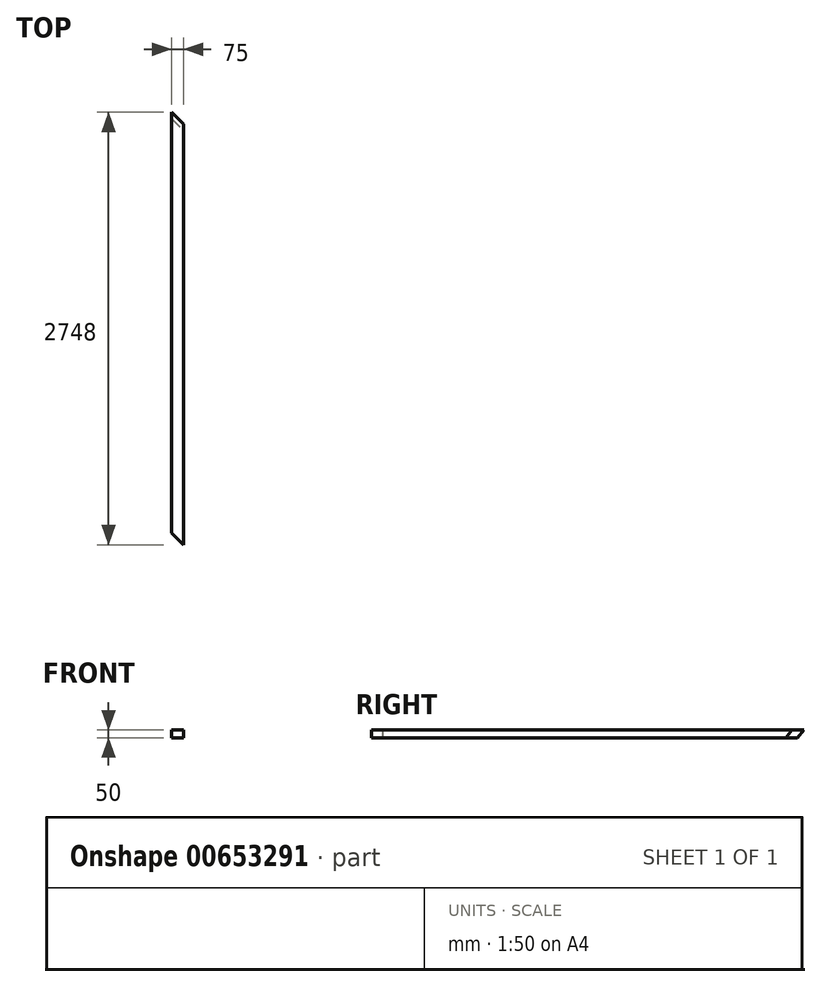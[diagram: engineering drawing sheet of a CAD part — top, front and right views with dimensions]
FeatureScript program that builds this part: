
annotation { "Feature Type Name" : "Feature", "Feature Type Description" : "" }
export const myFeature = defineFeature(function(context is Context, id is Id, definition is map)
    precondition{}
    {
        {
            var Q0;
            Q0=qCreatedBy(makeId("Front.planeOp"),FACE);
            var sketch = newSketch(context, id + "F0", { "sketchPlane" : qUnion([Q0])});
            skLineSegment(sketch, "E0.bottom", {"start": v(0, 0) * mm, "end": v(75, 0) * mm});
            skLineSegment(sketch, "E0.top", {"start": v(0, 50) * mm, "end": v(75, 50) * mm});
            skLineSegment(sketch, "E0.left", {"start": v(0, 0) * mm, "end": v(0, 50) * mm});
            skLineSegment(sketch, "E0.right", {"start": v(75, 0) * mm, "end": v(75, 50) * mm});
            skSolve(sketch);
        }
        {
            var Q0;
            Q0=makeQuery(id+"F0.imprint","IMPRINT",FACE,{"disambiguationData":[TD([[makeQuery(id+"F0.imprint","IMPRINT",EDGE,{"derivedFrom":sQuery(id+"F0.wireOp",EDGE,"E0.bottom")}),1.0]])]});
            extrude(context, id + "F1", {"entities" : qUnion([Q0]), "depth" : 2698 * mm + 50 * mm, "offsetDistance" : 25 * mm, "symmetric" : true});
        }
        {
            var Q0;
            Q0=makeQuery(id+"F1.opExtrude","SWEPT_FACE",FACE,{"disambiguationData":[OSD([sQuery(id+"F0.wireOp",EDGE,"E0.top")])]});
            var sketch = newSketch(context, id + "F2", { "sketchPlane" : qUnion([Q0])});
            skLineSegment(sketch, "E1", {"start": v(75, -1374) * mm, "end": v(0, -1299) * mm});
            skLineSegment(sketch, "E2.0", {"start": v(0, -1374) * mm, "end": v(75, -1374) * mm});
            skLineSegment(sketch, "E3.0", {"start": v(0, -1374) * mm, "end": v(0, 1374) * mm});
            skLineSegment(sketch, "E4", {"start": v(0, 1374) * mm, "end": v(75, 1299) * mm});
            skSolve(sketch);
        }
        {
            var Q0;
            {var subQ0=sQuery(id+"F2.wireOp",EDGE,"E4");Q0=makeQuery(id+"F2.imprint","IMPRINT",FACE,{"disambiguationData":[TD([[makeQuery(id+"F2.imprint","IMPRINT",EDGE,{"derivedFrom":subQ0}),1.0]])]});}
            var Q1;
            {var subQ0=sQuery(id+"F2.wireOp",EDGE,"E1");Q1=makeQuery(id+"F2.imprint","IMPRINT",FACE,{"disambiguationData":[TD([[makeQuery(id+"F2.imprint","IMPRINT",EDGE,{"derivedFrom":subQ0}),1.0]])]});}
            extrude(context, id + "F3", {"entities" : qUnion([Q0, Q1]), "operationType" : NewBodyOperationType.REMOVE, "endBound" : BoundingType.THROUGH_ALL, "oppositeDirection" : true, "depth" : 25 * mm, "offsetDistance" : 25 * mm});
        }
        {
            var Q0;
            Q0=makeQuery(id+"F1.opExtrude","SWEPT_FACE",FACE,{"disambiguationData":[OSD([sQuery(id+"F0.wireOp",EDGE,"E0.left")])]});
            var sketch = newSketch(context, id + "F4", { "sketchPlane" : qUnion([Q0])});
            skLineSegment(sketch, "E5", {"start": v(-1374, 50) * mm, "end": v(-1333.51, 0) * mm});
            skSolve(sketch);
        }
        {
            var Q0;
            {var subQ0=sQuery(id+"F4.wireOp",EDGE,"E5");Q0=makeQuery(id+"F4.imprint","IMPRINT",FACE,{"disambiguationData":[TD([[makeQuery(id+"F4.imprint","IMPRINT",EDGE,{"derivedFrom":subQ0}),-1.0]])]});}
            var Q1;
            Q1=makeQuery(id+"F3.boolean.opBoolean","INTERSECT",EDGE,{"derivedFrom":[makeQuery(id+"F1.opExtrude","SWEPT_FACE",FACE,{"disambiguationData":[OSD([sQuery(id+"F0.wireOp",EDGE,"E0.bottom")])]}),makeQuery(id+"F3.opExtrude","SWEPT_FACE",FACE,{"disambiguationData":[OSD([sQuery(id+"F2.wireOp",EDGE,"E4")])]})]});
            sweep(context, id + "F5", {"operationType" : NewBodyOperationType.REMOVE, "profiles" : qUnion([Q0]), "path" : qUnion([Q1])});
        }
    });
